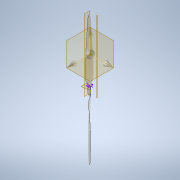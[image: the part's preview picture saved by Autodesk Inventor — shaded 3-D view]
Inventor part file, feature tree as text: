
AUTODESK INVENTOR PART (.ipt)
format: ipt  version: 2022 (Build 260153000, 153)  size: 3,324,416 bytes
history: native  units: mm
features: sketch x6, plane x3, mirror x2, loft x1, sweep x1, other x1
ambient origin geometry x8: Origin, YZ Plane, XZ Plane, XY Plane, X Axis, Y Axis, Z Axis, Center Point
bodies: Solid10 (feature_tree), Solid12 (feature_tree)
feature tree (14):
  sketch  "Sketch1"  dims[d3=30.0mm d27=20.0mm]
  sketch  "Sketch2"  dims[d33=7.5mm d34=2.0mm]
  plane  "Work Plane1"
  sketch  "3D Sketch1"
  sketch  "Sketch4"  dims[d35=0.0mm d36=90.0deg]
  plane  "Work Plane2"
  sketch  "Sketch6"  dims[d37=0.0mm d38=90.0deg]
  loft  "Loft1"
  plane  "Work Plane3"
  sweep  "Sweep13"
  mirror  "Mirror3"
  mirror  "Mirror4"
  sketch  "Sketch7"  dims[d39=-7.5mm d42=20.0mm d43=7.5mm d44=310.0mm d45=0.0mm d46=0.0mm]
  other  "Pattern of Solid10:2"
